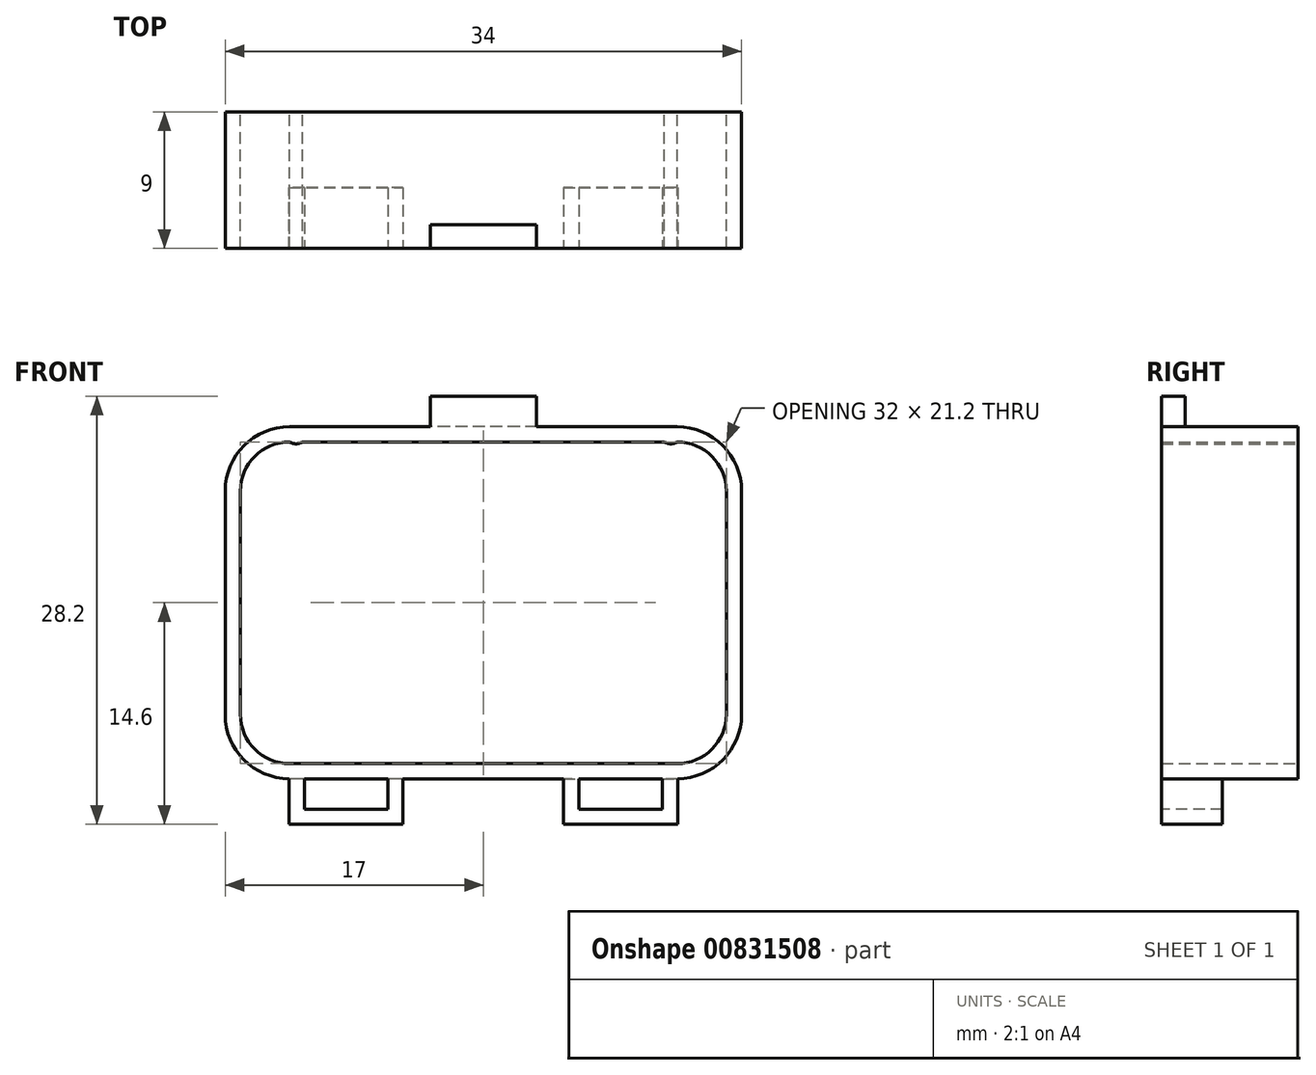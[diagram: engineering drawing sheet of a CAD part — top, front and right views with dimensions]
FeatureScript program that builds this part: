
annotation { "Feature Type Name" : "Feature", "Feature Type Description" : "" }
export const myFeature = defineFeature(function(context is Context, id is Id, definition is map)
    precondition{}
    {
        {
            var Q0;
            Q0=qCreatedBy(makeId("Front.planeOp"),FACE);
            var sketch = newSketch(context, id + "F0", { "sketchPlane" : qUnion([Q0])});
            skLineSegment(sketch, "E0.bottom", {"start": v(12.75, -10.6) * mm, "end": v(-12.75, -10.6) * mm});
            skLineSegment(sketch, "E0.top", {"start": v(12.75, 10.6) * mm, "end": v(-12.75, 10.6) * mm});
            skLineSegment(sketch, "E0.left", {"start": v(16, -7.35) * mm, "end": v(16, 7.35) * mm});
            skLineSegment(sketch, "E0.right", {"start": v(-16, -7.35) * mm, "end": v(-16, 7.35) * mm});
            skPoint(sketch, "E0.middle", {"position": v(0, 0) * mm});
            skPoint(sketch, "E1.visualSharp", {"position": v(-16, 10.6) * mm});
            skArc(sketch, "E1.filletArc", {"start": v(-12.75, 10.6) * mm, "mid": v(-15.05, 9.65) * mm, "end": v(-16, 7.35) * mm});
            skPoint(sketch, "E2.visualSharp", {"position": v(-16, -10.6) * mm});
            skArc(sketch, "E2.filletArc", {"start": v(-16, -7.35) * mm, "mid": v(-15.05, -9.65) * mm, "end": v(-12.75, -10.6) * mm});
            skPoint(sketch, "E3.visualSharp", {"position": v(16, -10.6) * mm});
            skArc(sketch, "E3.filletArc", {"start": v(12.75, -10.6) * mm, "mid": v(15.05, -9.65) * mm, "end": v(16, -7.35) * mm});
            skPoint(sketch, "E4.visualSharp", {"position": v(16, 10.6) * mm});
            skArc(sketch, "E4.filletArc", {"start": v(16, 7.35) * mm, "mid": v(15.05, 9.65) * mm, "end": v(12.75, 10.6) * mm});
            skArc(sketch, "E5.0", {"start": v(17, 7.35) * mm, "mid": v(15.76, 10.36) * mm, "end": v(12.75, 11.6) * mm});
            skLineSegment(sketch, "E5.1", {"start": v(17, -7.35) * mm, "end": v(17, 7.35) * mm});
            skLineSegment(sketch, "E5.2", {"start": v(12.75, 11.6) * mm, "end": v(-12.75, 11.6) * mm});
            skArc(sketch, "E5.3", {"start": v(12.75, -11.6) * mm, "mid": v(15.76, -10.36) * mm, "end": v(17, -7.35) * mm});
            skArc(sketch, "E5.4", {"start": v(-12.75, 11.6) * mm, "mid": v(-15.76, 10.36) * mm, "end": v(-17, 7.35) * mm});
            skLineSegment(sketch, "E5.5", {"start": v(-17, -7.35) * mm, "end": v(-17, 7.35) * mm});
            skArc(sketch, "E5.6", {"start": v(-17, -7.35) * mm, "mid": v(-15.76, -10.36) * mm, "end": v(-12.75, -11.6) * mm});
            skLineSegment(sketch, "E5.7", {"start": v(12.75, -11.6) * mm, "end": v(-12.75, -11.6) * mm});
            skSolve(sketch);
        }
        {
            var Q0;
            Q0=makeQuery(id+"F0.imprint","IMPRINT",FACE,{"disambiguationData":[TD([[makeQuery(id+"F0.imprint","IMPRINT",EDGE,{"derivedFrom":sQuery(id+"F0.wireOp",EDGE,"E0.bottom")}),1.0]])]});
            extrude(context, id + "F1", {"entities" : qUnion([Q0]), "depth" : 9 * mm, "offsetDistance" : 25 * mm});
        }
        {
            var Q0;
            Q0=makeQuery(id+"F1.opExtrude","SWEPT_FACE",FACE,{"disambiguationData":[OSD([sQuery(id+"F0.wireOp",EDGE,"E5.2")])]});
            var sketch = newSketch(context, id + "F2", { "sketchPlane" : qUnion([Q0])});
            skLineSegment(sketch, "E6.bottom", {"start": v(3.5, -7.44) * mm, "end": v(-3.5, -7.44) * mm});
            skLineSegment(sketch, "E6.top", {"start": v(3.5, -9) * mm, "end": v(-3.5, -9) * mm});
            skLineSegment(sketch, "E6.left", {"start": v(3.5, -7.44) * mm, "end": v(3.5, -9) * mm});
            skLineSegment(sketch, "E6.right", {"start": v(-3.5, -7.44) * mm, "end": v(-3.5, -9) * mm});
            skPoint(sketch, "E6.middle", {"position": v(0, -9) * mm});
            skSolve(sketch);
        }
        {
            var Q0;
            Q0 = qSketchRegion(id + "F2", true);
            extrude(context, id + "F3", {"entities" : qUnion([Q0]), "operationType" : NewBodyOperationType.ADD, "depth" : 2 * mm, "offsetDistance" : 25 * mm});
        }
        {
            var Q0;
            Q0=qCreatedBy(makeId("Front.planeOp"),FACE);
            cPlane(context, id + "F4", {"entities" : qUnion([Q0]), "cplaneType" : CPlaneType.OFFSET, "offset" : 9 * mm, "width" : 150 * mm, "height" : 150 * mm});
        }
        {
            var Q0;
            Q0=qCreatedBy(id+"F4.planeOp",FACE);
            var sketch = newSketch(context, id + "F5", { "sketchPlane" : qUnion([Q0])});
            skLineSegment(sketch, "E7", {"start": v(-12.79, -11.6) * mm, "end": v(-12.79, -14.6) * mm});
            skLineSegment(sketch, "E8", {"start": v(-12.79, -14.6) * mm, "end": v(-5.29, -14.6) * mm});
            skLineSegment(sketch, "E9", {"start": v(-5.29, -14.6) * mm, "end": v(-5.29, -11.6) * mm});
            skLineSegment(sketch, "E10", {"start": v(-5.29, -11.6) * mm, "end": v(-6.29, -11.6) * mm});
            skLineSegment(sketch, "E11", {"start": v(-6.29, -11.6) * mm, "end": v(-6.29, -13.6) * mm});
            skLineSegment(sketch, "E12", {"start": v(-6.29, -13.6) * mm, "end": v(-11.79, -13.6) * mm});
            skLineSegment(sketch, "E13", {"start": v(-11.79, -13.6) * mm, "end": v(-11.79, -11.6) * mm});
            skLineSegment(sketch, "E14", {"start": v(-11.79, -11.6) * mm, "end": v(-12.79, -11.6) * mm});
            skLineSegment(sketch, "E15.MirrorCS", {"start": v(11.79, -11.6) * mm, "end": v(12.79, -11.6) * mm});
            skLineSegment(sketch, "E16.MirrorCS", {"start": v(11.79, -13.6) * mm, "end": v(11.79, -11.6) * mm});
            skLineSegment(sketch, "E17.MirrorCS", {"start": v(5.29, -11.6) * mm, "end": v(6.29, -11.6) * mm});
            skLineSegment(sketch, "E18.MirrorCS", {"start": v(6.29, -13.6) * mm, "end": v(11.79, -13.6) * mm});
            skLineSegment(sketch, "E19.MirrorCS", {"start": v(6.29, -11.6) * mm, "end": v(6.29, -13.6) * mm});
            skLineSegment(sketch, "E20.MirrorCS", {"start": v(12.79, -14.6) * mm, "end": v(5.29, -14.6) * mm});
            skLineSegment(sketch, "E21.MirrorCS", {"start": v(5.29, -14.6) * mm, "end": v(5.29, -11.6) * mm});
            skLineSegment(sketch, "E22.MirrorCS", {"start": v(12.79, -11.6) * mm, "end": v(12.79, -14.6) * mm});
            skSolve(sketch);
        }
        {
            var Q0;
            Q0=makeQuery(id+"F5.imprint","IMPRINT",FACE,{"disambiguationData":[TD([[makeQuery(id+"F5.imprint","IMPRINT",EDGE,{"derivedFrom":sQuery(id+"F5.wireOp",EDGE,"E15.MirrorCS")}),-1.0]])]});
            var Q1;
            Q1=makeQuery(id+"F5.imprint","IMPRINT",FACE,{"disambiguationData":[TD([[makeQuery(id+"F5.imprint","IMPRINT",EDGE,{"derivedFrom":sQuery(id+"F5.wireOp",EDGE,"E7")}),1.0]])]});
            extrude(context, id + "F6", {"entities" : qUnion([Q0, Q1]), "operationType" : NewBodyOperationType.ADD, "oppositeDirection" : true, "depth" : 4 * mm, "offsetDistance" : 25 * mm});
        }
        {
            var Q0;
            Q0=qCreatedBy(makeId("Front.planeOp"),FACE);
            var sketch = newSketch(context, id + "F7", { "sketchPlane" : qUnion([Q0])});
            skArc(sketch, "E23", {"start": v(-12.75, 10.6) * mm, "mid": v(-12.33, 10.47) * mm, "end": v(-11.9, 10.6) * mm});
            skArc(sketch, "E24.MirrorCS", {"start": v(12.75, 10.6) * mm, "mid": v(12.33, 10.47) * mm, "end": v(11.9, 10.6) * mm});
            skLineSegment(sketch, "E25", {"start": v(-12.75, 10.6) * mm, "end": v(-11.9, 10.6) * mm});
            skLineSegment(sketch, "E26", {"start": v(11.9, 10.6) * mm, "end": v(12.75, 10.6) * mm});
            skSolve(sketch);
        }
        {
            var Q0;
            Q0 = qSketchRegion(id + "F7", true);
            extrude(context, id + "F8", {"entities" : qUnion([Q0]), "operationType" : NewBodyOperationType.ADD, "depth" : 9 * mm, "offsetDistance" : 25 * mm});
        }
        {
            var Q0;
            Q0 = qSketchRegion(id + "F7", true);
            extrude(context, id + "F9", {"entities" : qUnion([Q0]), "operationType" : NewBodyOperationType.ADD, "depth" : 9 * mm, "offsetDistance" : 25 * mm});
        }
    });
